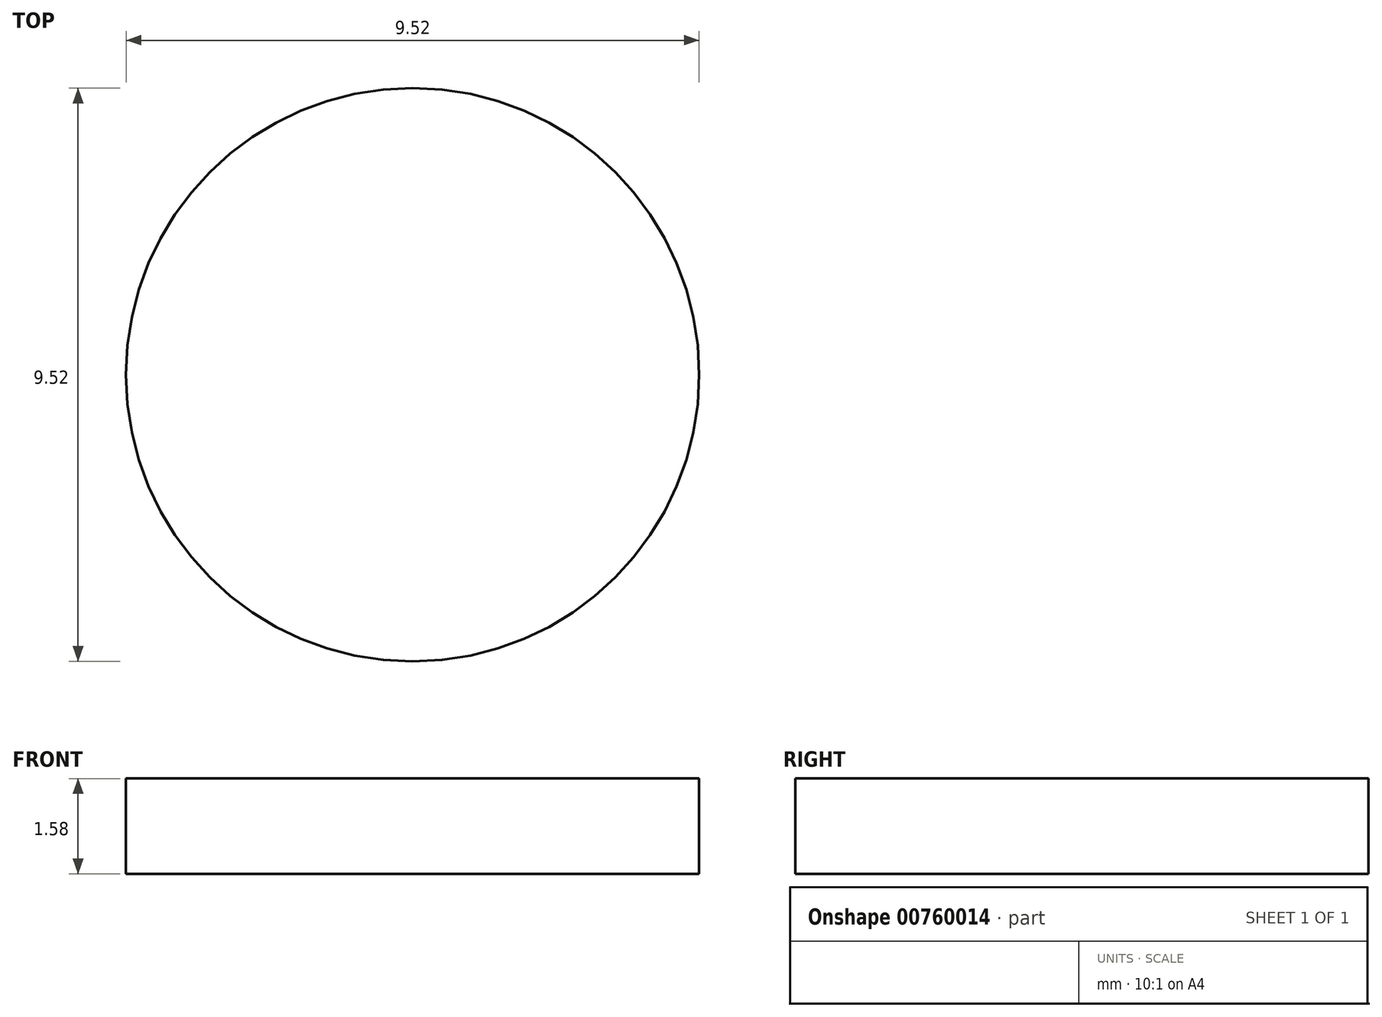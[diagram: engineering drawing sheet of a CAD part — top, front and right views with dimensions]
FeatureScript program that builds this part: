
annotation { "Feature Type Name" : "Feature", "Feature Type Description" : "" }
export const myFeature = defineFeature(function(context is Context, id is Id, definition is map)
    precondition{}
    {
        {
            var Q0;
            Q0=qCreatedBy(makeId("Top.planeOp"),FACE);
            var sketch = newSketch(context, id + "F0", { "sketchPlane" : qUnion([Q0])});
            skCircle(sketch, "E0", {"center": v(0, 0) * mm, "radius": 4.76 * mm});
            skSolve(sketch);
        }
        {
            var Q0;
            Q0=makeQuery(id+"F0.imprint","IMPRINT",FACE,{"disambiguationData":[TD([[makeQuery(id+"F0.imprint","IMPRINT",EDGE,{"derivedFrom":sQuery(id+"F0.wireOp",EDGE,"E0")}),1.0]])]});
            var Q1;
            Q1=qConstructionFilter(qBodyType(qCreatedBy(id+"F0",EDGE),BodyType.WIRE),ConstructionObject.NO);
            extrude(context, id + "F1", {"entities" : qUnion([Q0]), "surfaceEntities" : qUnion([Q1]), "endBound" : BoundingType.SYMMETRIC, "depth" : 1.59 * mm, "offsetDistance" : 25.4 * mm});
        }
    });
